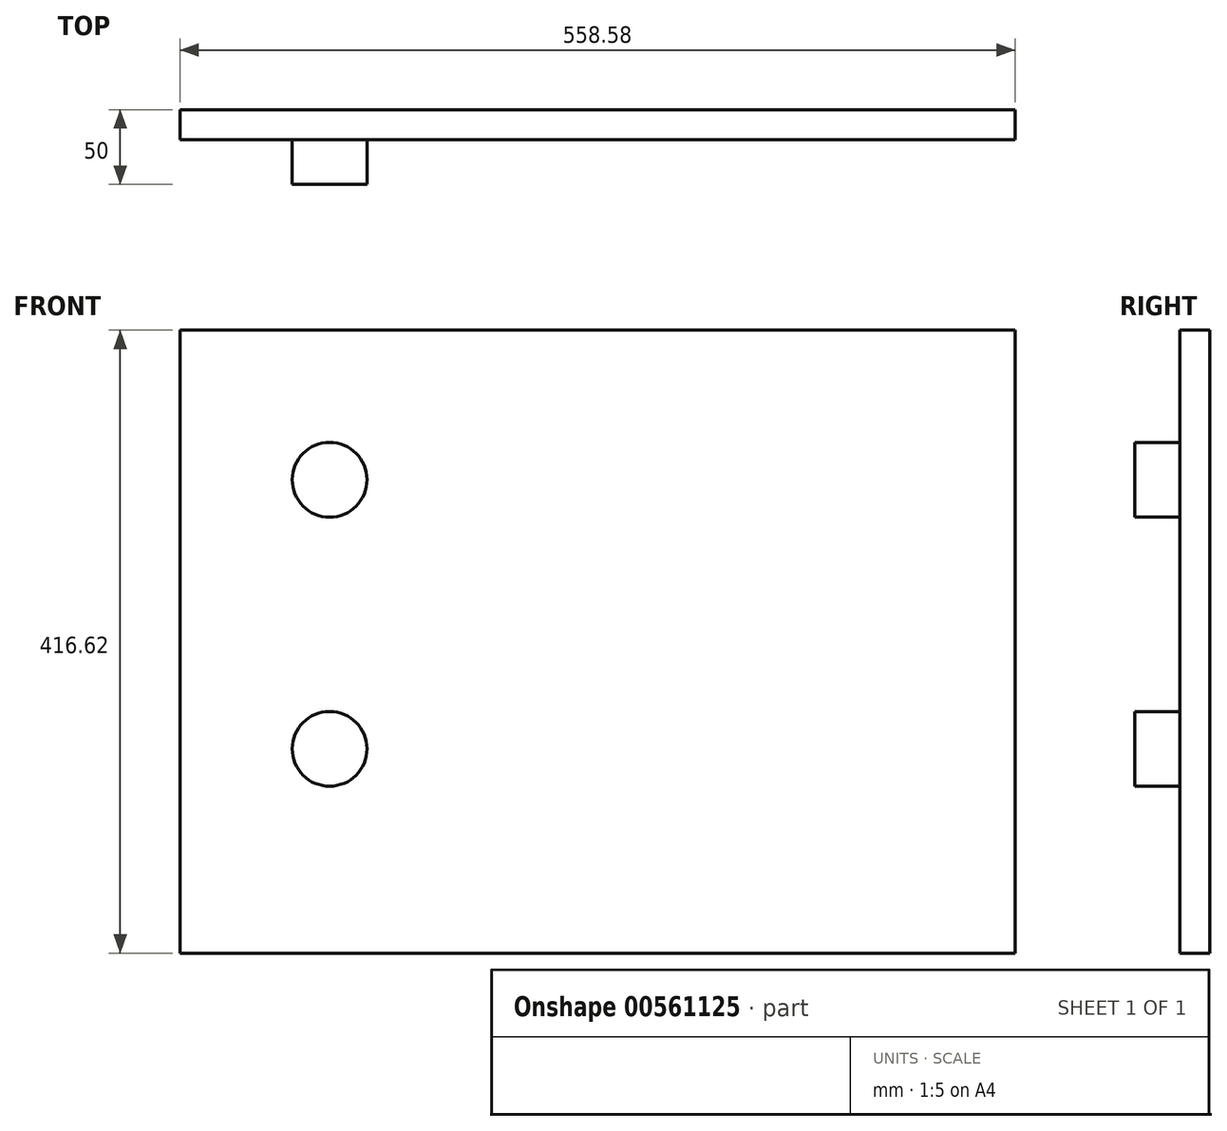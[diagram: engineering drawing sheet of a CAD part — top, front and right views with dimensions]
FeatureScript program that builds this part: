
annotation { "Feature Type Name" : "Feature", "Feature Type Description" : "" }
export const myFeature = defineFeature(function(context is Context, id is Id, definition is map)
    precondition{}
    {
        {
            var Q0;
            Q0=qCreatedBy(makeId("Front.planeOp"),FACE);
            var sketch = newSketch(context, id + "F0", { "sketchPlane" : qUnion([Q0])});
            skLineSegment(sketch, "E0.bottom", {"start": v(-276.06, 152.14) * mm, "end": v(282.52, 152.14) * mm});
            skLineSegment(sketch, "E0.top", {"start": v(-276.06, -264.48) * mm, "end": v(282.52, -264.48) * mm});
            skLineSegment(sketch, "E0.left", {"start": v(-276.06, 152.14) * mm, "end": v(-276.06, -264.48) * mm});
            skLineSegment(sketch, "E0.right", {"start": v(282.52, 152.14) * mm, "end": v(282.52, -264.48) * mm});
            skPoint(sketch, "E1", {"position": v(-176.06, 52.14) * mm});
            skCircle(sketch, "E2", {"center": v(-176.06, 52.14) * mm, "radius": 25 * mm});
            skCircle(sketch, "E3", {"center": v(-176.06, -127.86) * mm, "radius": 25 * mm});
            skLineSegment(sketch, "E4", {"start": v(-176.06, 52.14) * mm, "end": v(-176.06, -295.36) * mm, "construction": true});
            skSolve(sketch);
        }
        {
            var Q0;
            Q0=makeQuery(id+"F0.imprint","IMPRINT",FACE,{"disambiguationData":[TD([[makeQuery(id+"F0.imprint","IMPRINT",EDGE,{"derivedFrom":sQuery(id+"F0.wireOp",EDGE,"E0.bottom")}),-1.0]])]});
            var Q1;
            Q1=makeQuery(id+"F0.imprint","IMPRINT",FACE,{"disambiguationData":[TD([[makeQuery(id+"F0.imprint","IMPRINT",EDGE,{"derivedFrom":sQuery(id+"F0.wireOp",EDGE,"E2")}),1.0]])]});
            var Q2;
            Q2=makeQuery(id+"F0.imprint","IMPRINT",FACE,{"disambiguationData":[TD([[makeQuery(id+"F0.imprint","IMPRINT",EDGE,{"derivedFrom":sQuery(id+"F0.wireOp",EDGE,"E3")}),1.0]])]});
            extrude(context, id + "F1", {"entities" : qUnion([Q0, Q1, Q2]), "oppositeDirection" : true, "depth" : 20 * mm, "offsetDistance" : 25.4 * mm});
        }
        {
            var Q0;
            Q0=makeQuery(id+"F0.imprint","IMPRINT",FACE,{"disambiguationData":[TD([[makeQuery(id+"F0.imprint","IMPRINT",EDGE,{"derivedFrom":sQuery(id+"F0.wireOp",EDGE,"E2")}),1.0]])]});
            var Q1;
            Q1=makeQuery(id+"F0.imprint","IMPRINT",FACE,{"disambiguationData":[TD([[makeQuery(id+"F0.imprint","IMPRINT",EDGE,{"derivedFrom":sQuery(id+"F0.wireOp",EDGE,"E3")}),1.0]])]});
            extrude(context, id + "F2", {"entities" : qUnion([Q0, Q1]), "operationType" : NewBodyOperationType.ADD, "depth" : 30 * mm, "offsetDistance" : 25.4 * mm});
        }
    });
